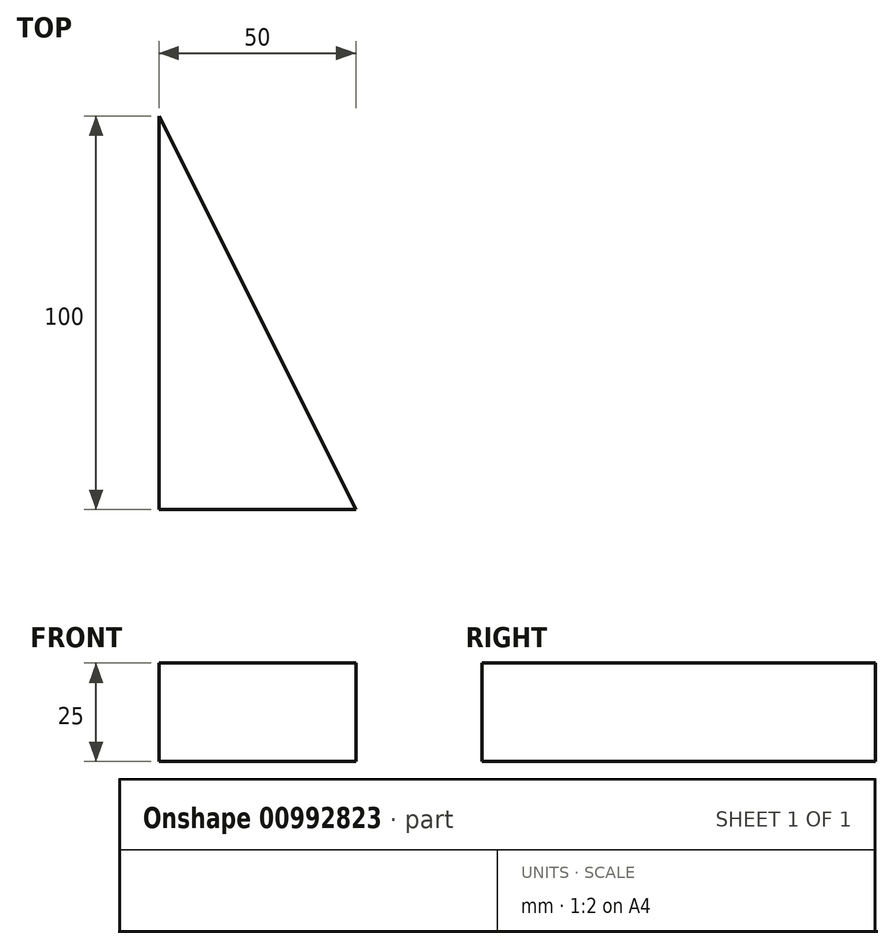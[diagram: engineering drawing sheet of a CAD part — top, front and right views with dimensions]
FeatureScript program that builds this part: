
annotation { "Feature Type Name" : "Feature", "Feature Type Description" : "" }
export const myFeature = defineFeature(function(context is Context, id is Id, definition is map)
    precondition{}
    {
        {
            assignVariable(context, id + "F0", {"name" : "Width", "anyValue" : 50 * mm});
        }
        {
            var Q0;
            Q0=qCreatedBy(makeId("Top.planeOp"),FACE);
            var sketch = newSketch(context, id + "F1", { "sketchPlane" : qUnion([Q0])});
            skLineSegment(sketch, "E0.bottom", {"start": v(0, 0) * mm, "end": v(50, 0) * mm});
            skLineSegment(sketch, "E0.top", {"start": v(0, 100) * mm, "end": v(50, 100) * mm, "construction": true});
            skLineSegment(sketch, "E0.left", {"start": v(0, 0) * mm, "end": v(0, 100) * mm});
            skLineSegment(sketch, "E0.right", {"start": v(50, 0) * mm, "end": v(50, 100) * mm, "construction": true});
            skLineSegment(sketch, "E1", {"start": v(0, 100) * mm, "end": v(50, 0) * mm});
            skSolve(sketch);
        }
        {
            var Q0;
            Q0=makeQuery(id+"F1.imprint","IMPRINT",FACE,{"disambiguationData":[TD([[makeQuery(id+"F1.imprint","IMPRINT",EDGE,{"derivedFrom":sQuery(id+"F1.wireOp",EDGE,"E0.bottom")}),1.0]])]});
            extrude(context, id + "F2", {"entities" : qUnion([Q0]), "depth" : getVariable(context, 'Width') * 0.5, "offsetDistance" : 25 * mm});
        }
    });
